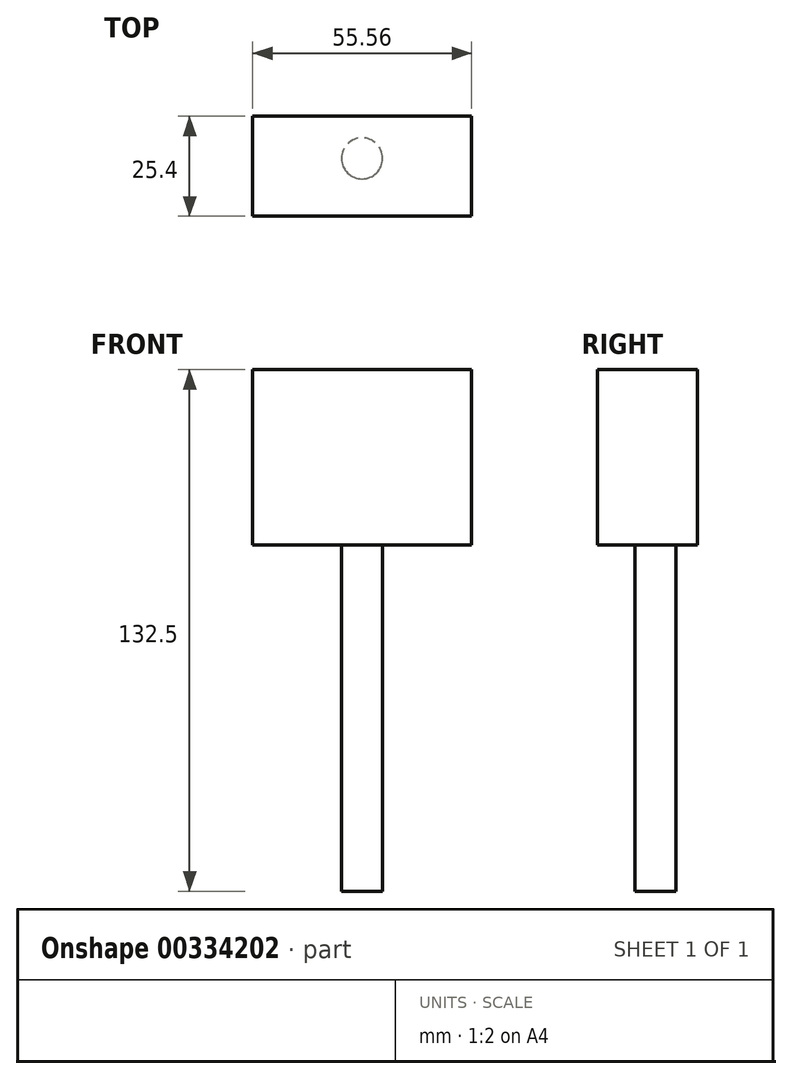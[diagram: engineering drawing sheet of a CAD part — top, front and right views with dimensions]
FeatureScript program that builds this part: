
annotation { "Feature Type Name" : "Feature", "Feature Type Description" : "" }
export const myFeature = defineFeature(function(context is Context, id is Id, definition is map)
    precondition{}
    {
        {
            var Q0;
            Q0=qCreatedBy(makeId("Front.planeOp"),FACE);
            var sketch = newSketch(context, id + "F0", { "sketchPlane" : qUnion([Q0])});
            skLineSegment(sketch, "E0.bottom", {"start": v(27.78, -22.28) * mm, "end": v(-27.78, -22.28) * mm});
            skLineSegment(sketch, "E0.top", {"start": v(27.78, 22.28) * mm, "end": v(-27.78, 22.28) * mm});
            skLineSegment(sketch, "E0.left", {"start": v(27.78, -22.28) * mm, "end": v(27.78, 22.28) * mm});
            skLineSegment(sketch, "E0.right", {"start": v(-27.78, -22.28) * mm, "end": v(-27.78, 22.28) * mm});
            skPoint(sketch, "E0.middle", {"position": v(0, 0) * mm});
            skSolve(sketch);
        }
        {
            var Q0;
            Q0=makeQuery(id+"F0.imprint","IMPRINT",FACE,{"disambiguationData":[TD([[makeQuery(id+"F0.imprint","IMPRINT",EDGE,{"derivedFrom":sQuery(id+"F0.wireOp",EDGE,"E0.bottom")}),-1.0]])]});
            extrude(context, id + "F1", {"entities" : qUnion([Q0]), "depth" : 25.4 * mm});
        }
        {
            var Q0;
            Q0=qCreatedBy(makeId("Top.planeOp"),FACE);
            var sketch = newSketch(context, id + "F2", { "sketchPlane" : qUnion([Q0])});
            skCircle(sketch, "E1", {"center": v(0, -10.7) * mm, "radius": 5.22 * mm});
            skSolve(sketch);
        }
        {
            var Q0;
            Q0 = qSketchRegion(id + "F2", true);
            extrude(context, id + "F3", {"entities" : qUnion([Q0]), "operationType" : NewBodyOperationType.ADD, "oppositeDirection" : true, "depth" : 110.22 * mm});
        }
    });
